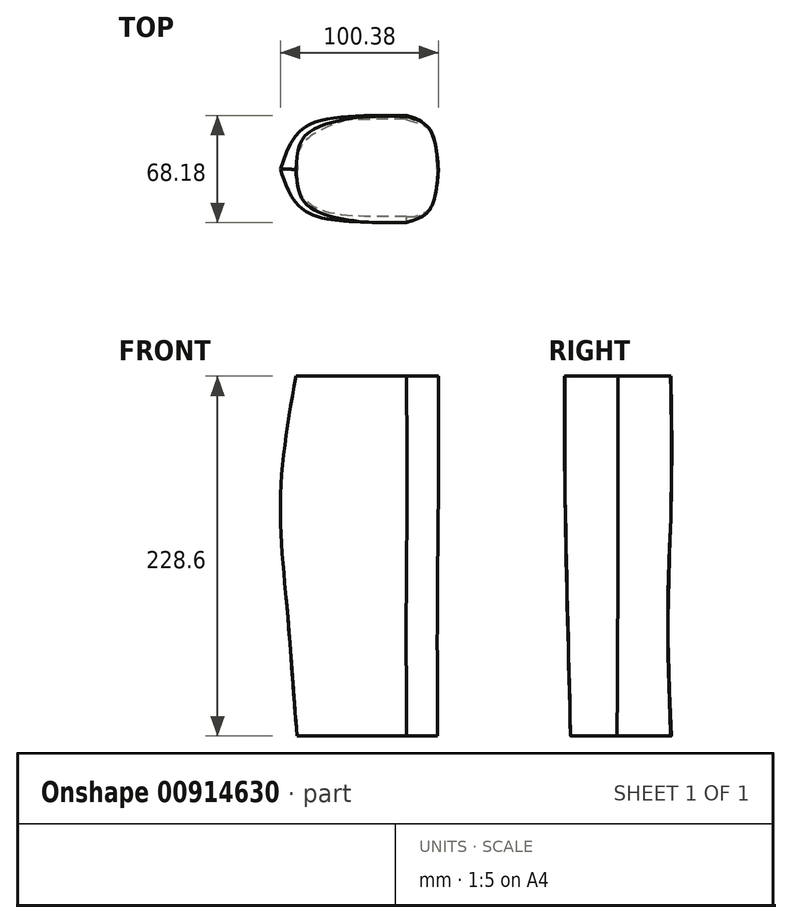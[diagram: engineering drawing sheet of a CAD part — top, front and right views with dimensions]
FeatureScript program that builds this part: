
annotation { "Feature Type Name" : "Feature", "Feature Type Description" : "" }
export const myFeature = defineFeature(function(context is Context, id is Id, definition is map)
    precondition{}
    {
        {
            var Q0;
            Q0=qCreatedBy(makeId("Top.planeOp"),FACE);
            var sketch = newSketch(context, id + "F0", { "sketchPlane" : qUnion([Q0])});
            skFitSpline(sketch, "E0", {"points": [v(33.04, 36.06) * mm, v(7.14, 36.06) * mm, v(-22.5, 26.96) * mm, v(-35.53, 14.66) * mm, v(-36.2, 2.01) * mm], "startDerivative": vector(-89.63, 1.21) * mm, "endDerivative": vector(6.96, -66.17) * mm});
            skFitSpline(sketch, "E1", {"points": [v(33.04, 36.06) * mm, v(46.56, 28.4) * mm, v(52.7, 2.01) * mm], "startDerivative": vector(36.98, 0.54) * mm, "endDerivative": vector(4.17, -56.31) * mm});
            skFitSpline(sketch, "E2.MirrorCS", {"points": [v(33.04, -27.44) * mm, v(7.14, -27.44) * mm, v(-22.5, -22.93) * mm, v(-35.53, -10.63) * mm, v(-36.2, 2.01) * mm], "startDerivative": vector(-89.63, -1.21) * mm, "endDerivative": vector(6.96, 66.17) * mm});
            skFitSpline(sketch, "E3.MirrorCS", {"points": [v(33.04, -27.44) * mm, v(46.56, -24.37) * mm, v(52.7, 2.01) * mm], "startDerivative": vector(36.98, -0.54) * mm, "endDerivative": vector(4.17, 56.31) * mm});
            skLineSegment(sketch, "E4", {"start": v(33.04, 36.06) * mm, "end": v(33.04, -27.44) * mm, "construction": true});
            skLineSegment(sketch, "E5", {"start": v(52.7, 2.01) * mm, "end": v(-36.2, 2.01) * mm, "construction": true});
            skSolve(sketch);
        }
        {
            var Q0;
            Q0=qCreatedBy(makeId("Top.planeOp"),FACE);
            cPlane(context, id + "F1", {"entities" : qUnion([Q0]), "cplaneType" : CPlaneType.OFFSET, "offset" : 76.2 * mm, "width" : 152.4 * mm, "height" : 152.4 * mm});
        }
        {
            var Q0;
            Q0=qCreatedBy(id+"F1.planeOp",FACE);
            var sketch = newSketch(context, id + "F2", { "sketchPlane" : qUnion([Q0])});
            skLineSegment(sketch, "E6", {"start": v(32.7, 34.24) * mm, "end": v(32.7, -29.26) * mm, "construction": true});
            skFitSpline(sketch, "E7", {"points": [v(32.7, 34.24) * mm, v(46.99, 28.02) * mm, v(52.45, 2.45) * mm], "startDerivative": vector(36.67, -13.62) * mm, "endDerivative": vector(3.67, -53.25) * mm});
            skFitSpline(sketch, "E8", {"points": [v(32.7, 34.24) * mm, v(7.05, 34.24) * mm, v(-13.35, 33.77) * mm, v(-33.18, 26) * mm, v(-42.37, 5.03) * mm, v(-42.37, 2.45) * mm], "startDerivative": vector(-108.74, 3.63) * mm, "endDerivative": vector(3.7, -23.22) * mm});
            skLineSegment(sketch, "E9", {"start": v(52.45, 2.45) * mm, "end": v(-42.37, 2.45) * mm, "construction": true});
            skFitSpline(sketch, "E10.MirrorCS", {"points": [v(32.7, -29.35) * mm, v(7.05, -29.35) * mm, v(-13.35, -28.87) * mm, v(-33.18, -21.11) * mm, v(-42.37, -0.14) * mm, v(-42.37, 2.45) * mm], "startDerivative": vector(-108.74, -3.63) * mm, "endDerivative": vector(3.7, 23.22) * mm});
            skFitSpline(sketch, "E11.MirrorCS", {"points": [v(32.7, -29.35) * mm, v(46.99, -23.13) * mm, v(52.45, 2.45) * mm], "startDerivative": vector(36.67, 13.62) * mm, "endDerivative": vector(3.67, 53.25) * mm});
            skSolve(sketch);
        }
        {
            var Q0;
            Q0=qCreatedBy(id+"F1.planeOp",FACE);
            cPlane(context, id + "F3", {"entities" : qUnion([Q0]), "cplaneType" : CPlaneType.OFFSET, "offset" : 76.2 * mm, "width" : 152.4 * mm, "height" : 152.4 * mm});
        }
        {
            var Q0;
            Q0=qCreatedBy(id+"F3.planeOp",FACE);
            var sketch = newSketch(context, id + "F4", { "sketchPlane" : qUnion([Q0])});
            skLineSegment(sketch, "E12", {"start": v(53.1, 2.73) * mm, "end": v(-47.06, 2.73) * mm, "construction": true});
            skLineSegment(sketch, "E13", {"start": v(33.24, 36.4) * mm, "end": v(33.24, -29.5) * mm, "construction": true});
            skFitSpline(sketch, "E14", {"points": [v(33.24, 36.4) * mm, v(47.46, 28.17) * mm, v(53.1, 2.73) * mm], "startDerivative": vector(37, -12.62) * mm, "endDerivative": vector(3.99, -53.17) * mm});
            skFitSpline(sketch, "E15", {"points": [v(33.24, 36.4) * mm, v(7.47, 36.4) * mm, v(-19.4, 33.86) * mm, v(-36.82, 24.55) * mm, v(-47.06, 2.73) * mm], "startDerivative": vector(-97.91, 1) * mm, "endDerivative": vector(-32.63, -98.04) * mm});
            skFitSpline(sketch, "E16.MirrorCS", {"points": [v(33.24, -30.94) * mm, v(7.47, -30.94) * mm, v(-19.4, -28.4) * mm, v(-36.82, -19.08) * mm, v(-47.06, 2.73) * mm], "startDerivative": vector(-97.91, -1) * mm, "endDerivative": vector(-32.63, 98.04) * mm});
            skFitSpline(sketch, "E17.MirrorCS", {"points": [v(33.24, -30.94) * mm, v(47.46, -22.7) * mm, v(53.1, 2.73) * mm], "startDerivative": vector(37, 12.62) * mm, "endDerivative": vector(3.99, 53.17) * mm});
            skSolve(sketch);
        }
        {
            var Q0;
            Q0=qCreatedBy(id+"F3.planeOp",FACE);
            cPlane(context, id + "F5", {"entities" : qUnion([Q0]), "cplaneType" : CPlaneType.OFFSET, "offset" : 76.2 * mm, "width" : 152.4 * mm, "height" : 152.4 * mm});
        }
        {
            var Q0;
            Q0=qCreatedBy(id+"F5.planeOp",FACE);
            var sketch = newSketch(context, id + "F6", { "sketchPlane" : qUnion([Q0])});
            skLineSegment(sketch, "E18", {"start": v(-37.4, 2.43) * mm, "end": v(53.17, 2.43) * mm, "construction": true});
            skLineSegment(sketch, "E19", {"start": v(32.81, -28.91) * mm, "end": v(32.81, 36) * mm, "construction": true});
            skFitSpline(sketch, "E20", {"points": [v(32.81, 36) * mm, v(47.06, 28.68) * mm, v(53.17, 2.43) * mm], "startDerivative": vector(37.5, -10.37) * mm, "endDerivative": vector(4.63, -54.87) * mm});
            skFitSpline(sketch, "E21", {"points": [v(32.81, 36) * mm, v(9.61, 36) * mm, v(-14.4, 32.34) * mm, v(-32.3, 22.78) * mm, v(-37.4, 2.43) * mm], "startDerivative": vector(-90.16, 2.6) * mm, "endDerivative": vector(-7.59, -93.89) * mm});
            skFitSpline(sketch, "E22.MirrorCS", {"points": [v(32.81, -31.15) * mm, v(9.61, -31.15) * mm, v(-14.4, -27.49) * mm, v(-32.3, -17.93) * mm, v(-37.4, 2.43) * mm], "startDerivative": vector(-90.16, -2.6) * mm, "endDerivative": vector(-7.59, 93.89) * mm});
            skFitSpline(sketch, "E23.MirrorCS", {"points": [v(32.81, -31.15) * mm, v(47.06, -23.83) * mm, v(53.17, 2.43) * mm], "startDerivative": vector(37.5, 10.37) * mm, "endDerivative": vector(4.63, 54.87) * mm});
            skSolve(sketch);
        }
        {
            var Q0;
            Q0=makeQuery(id+"F0.imprint","IMPRINT",FACE,{"disambiguationData":[TD([[makeQuery(id+"F0.imprint","IMPRINT",EDGE,{"derivedFrom":sQuery(id+"F0.wireOp",EDGE,"E0")}),1.0]])]});
            var Q1;
            Q1=makeQuery(id+"F2.imprint","IMPRINT",FACE,{"disambiguationData":[TD([[makeQuery(id+"F2.imprint","IMPRINT",EDGE,{"derivedFrom":sQuery(id+"F2.wireOp",EDGE,"E7")}),-1.0]])]});
            var Q2;
            Q2=makeQuery(id+"F4.imprint","IMPRINT",FACE,{"disambiguationData":[TD([[makeQuery(id+"F4.imprint","IMPRINT",EDGE,{"derivedFrom":sQuery(id+"F4.wireOp",EDGE,"E14")}),-1.0]])]});
            var Q3;
            Q3=makeQuery(id+"F6.imprint","IMPRINT",FACE,{"disambiguationData":[TD([[makeQuery(id+"F6.imprint","IMPRINT",EDGE,{"derivedFrom":sQuery(id+"F6.wireOp",EDGE,"E20")}),-1.0]])]});
            loft(context, id + "F7", {"sheetProfilesArray" : [{ "sheetProfileEntities" : qUnion([Q0]) }, { "sheetProfileEntities" : qUnion([Q1]) }, { "sheetProfileEntities" : qUnion([Q2]) }, { "sheetProfileEntities" : qUnion([Q3]) }]});
        }
    });
